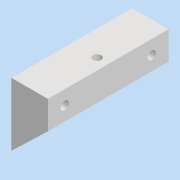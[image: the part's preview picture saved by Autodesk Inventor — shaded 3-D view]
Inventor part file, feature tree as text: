
AUTODESK INVENTOR PART (.ipt)
format: ipt  version: 2020 (Build 240168000, 168)  size: 131,584 bytes
history: native  units: mm
features: sketch x5, extrude x3, hole x2
ambient origin geometry x8: Origin, YZ Plane, XZ Plane, XY Plane, X Axis, Y Axis, Z Axis, Center Point
bodies: Solido1 (feature_tree)
feature tree (10):
  extrude  "Estrusione1"  Depth=26.0mm
  extrude  "Estrusione2"  Depth=86.0mm
  extrude  "Estrusione3"  Depth=20.0mm TaperAngle=0.0deg
  hole  "Foro1"  [1 undecoded]
  hole  "Foro2"  [1 undecoded]
  sketch  "Schizzo1"
  sketch  "Schizzo2"
  sketch  "Schizzo3"
  sketch  "Schizzo4"
  sketch  "Schizzo5"
note: 2 required parameter values undecoded (feature->parameter linkage not recoverable at this tier; creation-order binding heuristic only, values carry confidence <= 0.55)
